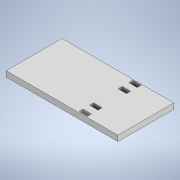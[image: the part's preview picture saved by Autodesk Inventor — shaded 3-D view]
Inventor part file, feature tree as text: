
AUTODESK INVENTOR PART (.ipt)
format: ipt  version: 2022 (Build 260153000, 153)  size: 120,320 bytes
history: native  units: mm
features: extrude x2, sketch x2
ambient origin geometry x8: Origin, YZ Plane, XZ Plane, XY Plane, X Axis, Y Axis, Z Axis, Center Point
bodies: Solid1 (feature_tree)
feature tree (4):
  extrude  "Extrusion1"  Depth=100.0mm
  extrude  "Extrusion2"  Depth=15.0mm
  sketch  "Sketch1"  dims[d0=200.0mm d1=100.0mm]
  sketch  "Sketch2"  dims[d2=10.0mm d3=0.0mm d5=15.0mm d6=7.0mm d9=25.0mm d10=0.0mm d11=2.0mm d12=6.0mm]
